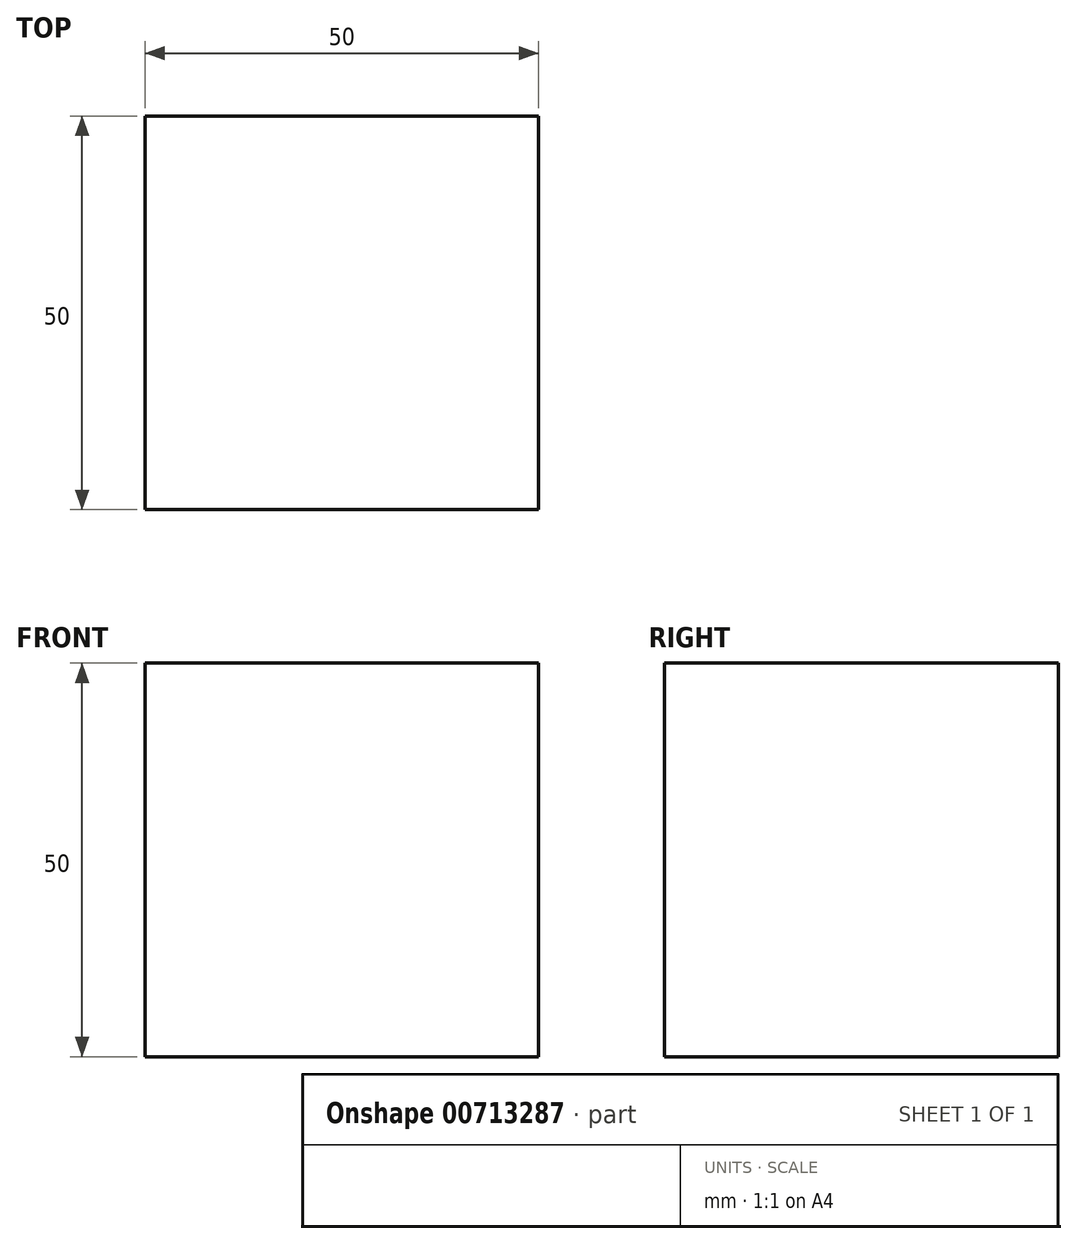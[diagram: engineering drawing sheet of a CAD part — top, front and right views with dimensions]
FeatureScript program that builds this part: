
annotation { "Feature Type Name" : "Feature", "Feature Type Description" : "" }
export const myFeature = defineFeature(function(context is Context, id is Id, definition is map)
    precondition{}
    {
        {
            var Q0;
            Q0=qCreatedBy(makeId("Front.planeOp"),FACE);
            var sketch = newSketch(context, id + "F0", { "sketchPlane" : qUnion([Q0])});
            skLineSegment(sketch, "E0.bottom", {"start": v(25, 25) * mm, "end": v(-25, 25) * mm});
            skLineSegment(sketch, "E0.top", {"start": v(25, -25) * mm, "end": v(-25, -25) * mm});
            skLineSegment(sketch, "E0.left", {"start": v(25, 25) * mm, "end": v(25, -25) * mm});
            skLineSegment(sketch, "E0.right", {"start": v(-25, 25) * mm, "end": v(-25, -25) * mm});
            skPoint(sketch, "E0.middle", {"position": v(0, 0) * mm});
            skSolve(sketch);
        }
        {
            var Q0;
            Q0=makeQuery(id+"F0.imprint","IMPRINT",FACE,{"disambiguationData":[TD([[makeQuery(id+"F0.imprint","IMPRINT",EDGE,{"derivedFrom":sQuery(id+"F0.wireOp",EDGE,"E0.bottom")}),1.0]])]});
            extrude(context, id + "F1", {"entities" : qUnion([Q0]), "oppositeDirection" : true, "depth" : 50 * mm, "offsetDistance" : 25 * mm});
        }
    });
